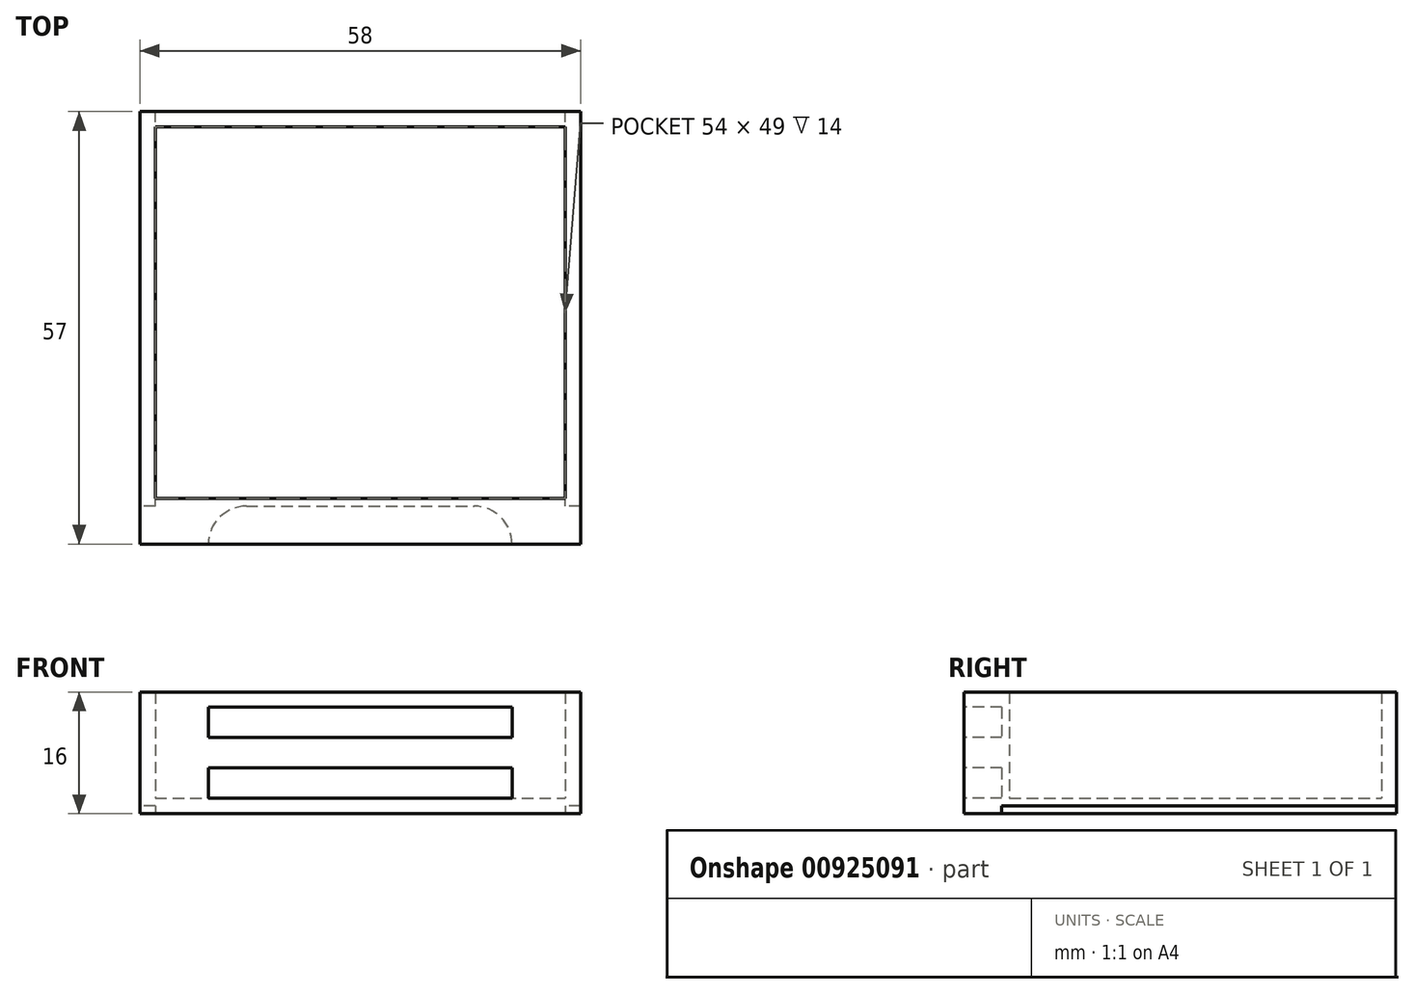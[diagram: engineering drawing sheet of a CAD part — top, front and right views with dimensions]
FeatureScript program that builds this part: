
annotation { "Feature Type Name" : "Feature", "Feature Type Description" : "" }
export const myFeature = defineFeature(function(context is Context, id is Id, definition is map)
    precondition{}
    {
        {
            var Q0;
            Q0=qCreatedBy(makeId("Front.planeOp"),FACE);
            var sketch = newSketch(context, id + "F0", { "sketchPlane" : qUnion([Q0])});
            skLineSegment(sketch, "E0.bottom", {"start": v(-61.54, 21.4) * mm, "end": v(-3.54, 21.4) * mm});
            skLineSegment(sketch, "E0.top", {"start": v(-61.54, 5.4) * mm, "end": v(-3.54, 5.4) * mm});
            skLineSegment(sketch, "E0.left", {"start": v(-61.54, 21.4) * mm, "end": v(-61.54, 5.4) * mm});
            skLineSegment(sketch, "E0.right", {"start": v(-3.54, 21.4) * mm, "end": v(-3.54, 5.4) * mm});
            skLineSegment(sketch, "E1.bottom", {"start": v(-59.54, 21.4) * mm, "end": v(-5.54, 21.4) * mm});
            skLineSegment(sketch, "E1.top", {"start": v(-59.54, 7.4) * mm, "end": v(-5.54, 7.4) * mm});
            skLineSegment(sketch, "E1.left", {"start": v(-59.54, 21.4) * mm, "end": v(-59.54, 7.4) * mm});
            skLineSegment(sketch, "E1.right", {"start": v(-5.54, 21.4) * mm, "end": v(-5.54, 7.4) * mm});
            skSolve(sketch);
        }
        {
            var Q0;
            Q0=makeQuery(id+"F0.imprint","IMPRINT",FACE,{"disambiguationData":[TD([[makeQuery(id+"F0.imprint","IMPRINT",EDGE,{"derivedFrom":sQuery(id+"F0.wireOp",EDGE,"E0.top")}),1.0]])]});
            extrude(context, id + "F1", {"entities" : qUnion([Q0]), "depth" : 57 * mm, "offsetDistance" : 25 * mm});
        }
        {
            var Q0;
            Q0=makeQuery(id+"F0.imprint","IMPRINT",FACE,{"disambiguationData":[TD([[makeQuery(id+"F0.imprint","IMPRINT",EDGE,{"derivedFrom":sQuery(id+"F0.wireOp",EDGE,"E1.top")}),1.0]])]});
            extrude(context, id + "F2", {"entities" : qUnion([Q0]), "operationType" : NewBodyOperationType.ADD, "depth" : 2 * mm, "offsetDistance" : 25 * mm});
        }
        {
            var Q0;
            Q0=makeQuery(id+"F0.imprint","IMPRINT",FACE,{"disambiguationData":[TD([[makeQuery(id+"F0.imprint","IMPRINT",EDGE,{"derivedFrom":sQuery(id+"F0.wireOp",EDGE,"E1.top")}),1.0]])]});
            extrude(context, id + "F3", {"entities" : qUnion([Q0]), "operationType" : NewBodyOperationType.ADD, "depth" : 57 * mm, "offsetDistance" : 25 * mm, "hasSecondDirection" : true, "secondDirectionOppositeDirection" : false, "secondDirectionDepth" : 51 * mm});
        }
        {
            var Q0;
            {var subQ0=sQuery(id+"F0.wireOp",EDGE,"E1.right");var subQ1=sQuery(id+"F0.wireOp",EDGE,"E1.left");var subQ2=sQuery(id+"F0.wireOp",EDGE,"E1.top");var subQ3=sQuery(id+"F0.wireOp",EDGE,"E0.bottom");Q0=makeQuery(id+"F3.boolean.opBoolean","MERGE",FACE,{"derivedFrom":[makeQuery(id+"F1.opExtrude","CAP_FACE",FACE,{"disambiguationData":[OSD([subQ3,sQuery(id+"F0.wireOp",EDGE,"E0.top"),sQuery(id+"F0.wireOp",EDGE,"E0.left"),sQuery(id+"F0.wireOp",EDGE,"E0.right"),subQ2,subQ1,subQ0])],"isStart":false}),makeQuery(id+"F3.opExtrude","CAP_FACE",FACE,{"disambiguationData":[OSD([subQ3,subQ2,subQ1,subQ0])],"isStart":false})]});}
            var sketch = newSketch(context, id + "F4", { "sketchPlane" : qUnion([Q0])});
            skLineSegment(sketch, "E2.bottom", {"start": v(-52.54, 19.4) * mm, "end": v(-12.54, 19.4) * mm});
            skLineSegment(sketch, "E2.top", {"start": v(-52.54, 7.4) * mm, "end": v(-12.54, 7.4) * mm});
            skLineSegment(sketch, "E2.left", {"start": v(-52.54, 19.4) * mm, "end": v(-52.54, 7.4) * mm});
            skLineSegment(sketch, "E2.right", {"start": v(-12.54, 19.4) * mm, "end": v(-12.54, 7.4) * mm});
            skLineSegment(sketch, "E3.bottom", {"start": v(-52.54, 15.4) * mm, "end": v(-12.54, 15.4) * mm});
            skLineSegment(sketch, "E3.top", {"start": v(-52.54, 11.4) * mm, "end": v(-12.54, 11.4) * mm});
            skLineSegment(sketch, "E3.left", {"start": v(-52.54, 15.4) * mm, "end": v(-52.54, 11.4) * mm});
            skLineSegment(sketch, "E3.right", {"start": v(-12.54, 15.4) * mm, "end": v(-12.54, 11.4) * mm});
            skLineSegment(sketch, "E4", {"start": v(-12.54, 17.48) * mm, "end": v(-3.54, 17.48) * mm, "construction": true});
            skLineSegment(sketch, "E5", {"start": v(-52.54, 17.48) * mm, "end": v(-61.54, 17.48) * mm, "construction": true});
            skLineSegment(sketch, "E6", {"start": v(-37.8, 7.4) * mm, "end": v(-37.8, 5.4) * mm, "construction": true});
            skLineSegment(sketch, "E7", {"start": v(-37.8, 19.4) * mm, "end": v(-37.8, 21.4) * mm, "construction": true});
            skLineSegment(sketch, "E8", {"start": v(-12.4, 15.4) * mm, "end": v(-12.4, 19.4) * mm, "construction": true});
            skLineSegment(sketch, "E9", {"start": v(-12.4, 11.4) * mm, "end": v(-12.4, 7.4) * mm, "construction": true});
            skSolve(sketch);
        }
        {
            var Q0;
            {var subQ0=sQuery(id+"F4.wireOp",EDGE,"E2.bottom");Q0=makeQuery(id+"F4.imprint","IMPRINT",FACE,{"disambiguationData":[TD([[makeQuery(id+"F4.imprint","IMPRINT",EDGE,{"derivedFrom":subQ0}),-1.0]])]});}
            var Q1;
            {var subQ0=sQuery(id+"F4.wireOp",EDGE,"E2.top");Q1=makeQuery(id+"F4.imprint","IMPRINT",FACE,{"disambiguationData":[TD([[makeQuery(id+"F4.imprint","IMPRINT",EDGE,{"derivedFrom":subQ0}),1.0]])]});}
            extrude(context, id + "F5", {"entities" : qUnion([Q0, Q1]), "operationType" : NewBodyOperationType.REMOVE, "oppositeDirection" : true, "depth" : 5 * mm, "offsetDistance" : 25 * mm});
        }
        {
            var Q0;
            Q0=makeQuery(id+"F5.boolean.opBoolean","COPY",EDGE,{"derivedFrom":makeQuery(id+"F5.opExtrude","CAP_EDGE",EDGE,{"disambiguationData":[OSD([sQuery(id+"F4.wireOp",EDGE,"E2.left")])],"isStart":false})});
            var Q1;
            Q1=makeQuery(id+"F5.boolean.opBoolean","COPY",EDGE,{"derivedFrom":makeQuery(id+"F5.opExtrude","CAP_EDGE",EDGE,{"disambiguationData":[OSD([sQuery(id+"F4.wireOp",EDGE,"E2.right")])],"isStart":false})});
            fillet(context, id + "F6", {"entities" : qUnion([Q0, Q1]), "radius" : 5 * mm, "tangentPropagation" : true, "allowEdgeOverflow" : false});
        }
        {
            var Q0;
            Q0=makeQuery(id+"F1.opExtrude","SWEPT_FACE",FACE,{"disambiguationData":[OSD([sQuery(id+"F0.wireOp",EDGE,"E0.left")])]});
            var sketch = newSketch(context, id + "F7", { "sketchPlane" : qUnion([Q0])});
            skLineSegment(sketch, "E10.bottom", {"start": v(0, 5.4) * mm, "end": v(52, 5.4) * mm});
            skLineSegment(sketch, "E10.top", {"start": v(0, 6.4) * mm, "end": v(52, 6.4) * mm});
            skLineSegment(sketch, "E10.left", {"start": v(0, 5.4) * mm, "end": v(0, 6.4) * mm});
            skLineSegment(sketch, "E10.right", {"start": v(52, 5.4) * mm, "end": v(52, 6.4) * mm});
            skSolve(sketch);
        }
        {
            var Q0;
            Q0=makeQuery(id+"F7.imprint","IMPRINT",FACE,{"disambiguationData":[TD([[makeQuery(id+"F7.imprint","IMPRINT",EDGE,{"derivedFrom":sQuery(id+"F7.wireOp",EDGE,"E10.bottom")}),-1.0]])]});
            extrude(context, id + "F8", {"entities" : qUnion([Q0]), "operationType" : NewBodyOperationType.REMOVE, "oppositeDirection" : true, "depth" : 2 * mm, "offsetDistance" : 25 * mm});
        }
        {
            var Q0;
            Q0=makeQuery(id+"F7.imprint","IMPRINT",FACE,{"disambiguationData":[TD([[makeQuery(id+"F7.imprint","IMPRINT",EDGE,{"derivedFrom":sQuery(id+"F7.wireOp",EDGE,"E10.bottom")}),-1.0]])]});
            extrude(context, id + "F9", {"entities" : qUnion([Q0]), "operationType" : NewBodyOperationType.REMOVE, "oppositeDirection" : true, "depth" : 58 * mm, "offsetDistance" : 25 * mm, "hasSecondDirection" : true, "secondDirectionOppositeDirection" : true, "secondDirectionDepth" : 56 * mm});
        }
    });
